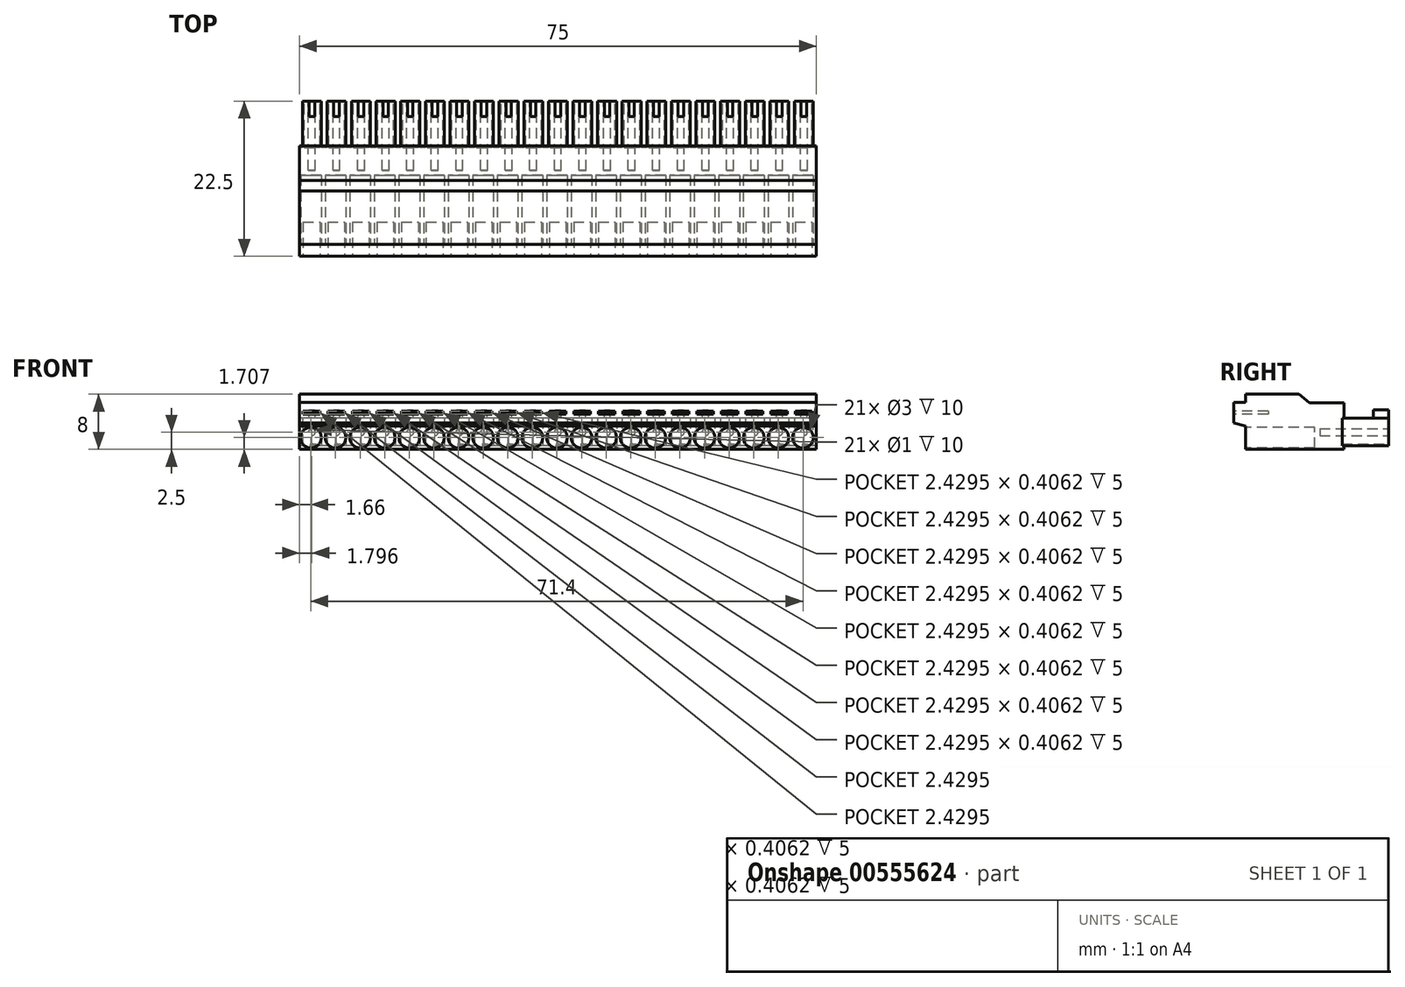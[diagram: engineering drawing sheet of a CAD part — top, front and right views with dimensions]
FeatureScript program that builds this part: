
annotation { "Feature Type Name" : "Feature", "Feature Type Description" : "" }
export const myFeature = defineFeature(function(context is Context, id is Id, definition is map)
    precondition{}
    {
        {
            var Q0;
            Q0=qCreatedBy(makeId("Right.planeOp"),FACE);
            var sketch = newSketch(context, id + "F0", { "sketchPlane" : qUnion([Q0])});
            skLineSegment(sketch, "E0", {"start": v(0, 0) * mm, "end": v(-14.25, 0) * mm});
            skLineSegment(sketch, "E1", {"start": v(-14.25, 0) * mm, "end": v(-14.25, 3.41) * mm});
            skLineSegment(sketch, "E2", {"start": v(-14.25, 8) * mm, "end": v(-6.5, 8) * mm});
            skLineSegment(sketch, "E3", {"start": v(0, 0) * mm, "end": v(0, 6.75) * mm});
            skLineSegment(sketch, "E4", {"start": v(0, 6.75) * mm, "end": v(-5, 6.75) * mm});
            skLineSegment(sketch, "E5", {"start": v(-5, 6.75) * mm, "end": v(-6.5, 8) * mm});
            skPoint(sketch, "E6.orphan", {"position": v(-5, 8) * mm});
            skLineSegment(sketch, "E7", {"start": v(-16, 3.83) * mm, "end": v(-16, 6.83) * mm});
            skLineSegment(sketch, "E8", {"start": v(-16, 6.83) * mm, "end": v(-14.25, 6.83) * mm});
            skLineSegment(sketch, "E9", {"start": v(-16, 3.83) * mm, "end": v(-14.25, 3.41) * mm});
            skLineSegment(sketch, "E10.trimOffspring", {"start": v(-14.25, 6.83) * mm, "end": v(-14.25, 8) * mm});
            skPoint(sketch, "E11.orphan", {"position": v(-14.25, 4) * mm});
            skLineSegment(sketch, "E12", {"start": v(0, 0) * mm, "end": v(0, 0.5) * mm});
            skLineSegment(sketch, "E13", {"start": v(0, 0.5) * mm, "end": v(6.5, 0.5) * mm});
            skLineSegment(sketch, "E14", {"start": v(6.5, 0.5) * mm, "end": v(6.5, 4.5) * mm});
            skLineSegment(sketch, "E15", {"start": v(6.5, 4.5) * mm, "end": v(0, 4.5) * mm});
            skSolve(sketch);
        }
        {
            var Q0;
            Q0 = qSketchRegion(id + "F0", true);
            extrude(context, id + "F1", {"entities" : qUnion([Q0]), "depth" : 75 * mm, "offsetDistance" : 25 * mm});
        }
        {
            var Q0;
            Q0=makeQuery(id+"F1.opExtrude","SWEPT_FACE",FACE,{"disambiguationData":[OSD([sQuery(id+"F0.wireOp",EDGE,"E1")])]});
            var sketch = newSketch(context, id + "F2", { "sketchPlane" : qUnion([Q0])});
            skLineSegment(sketch, "E16", {"start": v(0, 1.7) * mm, "end": v(75, 1.7) * mm, "construction": true});
            skCircle(sketch, "E17", {"center": v(1.66, 1.7) * mm, "radius": 1.5 * mm});
            skCircle(sketch, "E18.1.0.0", {"center": v(5.23, 1.7) * mm, "radius": 1.5 * mm});
            skCircle(sketch, "E18.2.0.0", {"center": v(8.8, 1.7) * mm, "radius": 1.5 * mm});
            skCircle(sketch, "E18.3.0.0", {"center": v(12.37, 1.7) * mm, "radius": 1.5 * mm});
            skCircle(sketch, "E18.4.0.0", {"center": v(15.94, 1.7) * mm, "radius": 1.5 * mm});
            skCircle(sketch, "E18.5.0.0", {"center": v(19.51, 1.7) * mm, "radius": 1.5 * mm});
            skCircle(sketch, "E18.6.0.0", {"center": v(23.08, 1.7) * mm, "radius": 1.5 * mm});
            skCircle(sketch, "E18.7.0.0", {"center": v(26.65, 1.7) * mm, "radius": 1.5 * mm});
            skCircle(sketch, "E18.8.0.0", {"center": v(30.22, 1.7) * mm, "radius": 1.5 * mm});
            skCircle(sketch, "E18.9.0.0", {"center": v(33.8, 1.7) * mm, "radius": 1.5 * mm});
            skCircle(sketch, "E18.10.0.0", {"center": v(37.36, 1.7) * mm, "radius": 1.5 * mm});
            skCircle(sketch, "E18.11.0.0", {"center": v(40.93, 1.7) * mm, "radius": 1.5 * mm});
            skCircle(sketch, "E18.12.0.0", {"center": v(44.5, 1.7) * mm, "radius": 1.5 * mm});
            skCircle(sketch, "E18.13.0.0", {"center": v(48.07, 1.7) * mm, "radius": 1.5 * mm});
            skCircle(sketch, "E18.14.0.0", {"center": v(51.64, 1.7) * mm, "radius": 1.5 * mm});
            skCircle(sketch, "E18.15.0.0", {"center": v(55.21, 1.7) * mm, "radius": 1.5 * mm});
            skCircle(sketch, "E18.16.0.0", {"center": v(58.78, 1.7) * mm, "radius": 1.5 * mm});
            skCircle(sketch, "E18.17.0.0", {"center": v(62.35, 1.7) * mm, "radius": 1.5 * mm});
            skCircle(sketch, "E18.18.0.0", {"center": v(65.92, 1.7) * mm, "radius": 1.5 * mm});
            skCircle(sketch, "E18.19.0.0", {"center": v(69.5, 1.7) * mm, "radius": 1.5 * mm});
            skCircle(sketch, "E18.20.0.0", {"center": v(73.06, 1.7) * mm, "radius": 1.5 * mm});
            skLineSegment(sketch, "E18.direction1", {"start": v(1.66, 1.7) * mm, "end": v(5.23, 1.7) * mm, "construction": true});
            skSolve(sketch);
        }
        {
            var Q0;
            Q0 = qSketchRegion(id + "F2", true);
            extrude(context, id + "F3", {"entities" : qUnion([Q0]), "operationType" : NewBodyOperationType.REMOVE, "oppositeDirection" : true, "depth" : 10 * mm, "offsetDistance" : 25 * mm});
        }
        {
            var Q0;
            Q0=makeQuery(id+"F1.opExtrude","SWEPT_FACE",FACE,{"disambiguationData":[OSD([sQuery(id+"F0.wireOp",EDGE,"E14")])]});
            var sketch = newSketch(context, id + "F4", { "sketchPlane" : qUnion([Q0])});
            skLineSegment(sketch, "E19", {"start": v(-75, 2.5) * mm, "end": v(0, 2.5) * mm, "construction": true});
            skCircle(sketch, "E20", {"center": v(-73.2, 2.5) * mm, "radius": 0.5 * mm});
            skCircle(sketch, "E21.1.0.0", {"center": v(-69.63, 2.5) * mm, "radius": 0.5 * mm});
            skCircle(sketch, "E21.2.0.0", {"center": v(-66.06, 2.5) * mm, "radius": 0.5 * mm});
            skCircle(sketch, "E21.3.0.0", {"center": v(-62.49, 2.5) * mm, "radius": 0.5 * mm});
            skCircle(sketch, "E21.4.0.0", {"center": v(-58.92, 2.5) * mm, "radius": 0.5 * mm});
            skCircle(sketch, "E21.5.0.0", {"center": v(-55.35, 2.5) * mm, "radius": 0.5 * mm});
            skCircle(sketch, "E21.6.0.0", {"center": v(-51.78, 2.5) * mm, "radius": 0.5 * mm});
            skCircle(sketch, "E21.7.0.0", {"center": v(-48.2, 2.5) * mm, "radius": 0.5 * mm});
            skCircle(sketch, "E21.8.0.0", {"center": v(-44.64, 2.5) * mm, "radius": 0.5 * mm});
            skCircle(sketch, "E21.9.0.0", {"center": v(-41.07, 2.5) * mm, "radius": 0.5 * mm});
            skCircle(sketch, "E21.10.0.0", {"center": v(-37.5, 2.5) * mm, "radius": 0.5 * mm});
            skCircle(sketch, "E21.11.0.0", {"center": v(-33.93, 2.5) * mm, "radius": 0.5 * mm});
            skCircle(sketch, "E21.12.0.0", {"center": v(-30.36, 2.5) * mm, "radius": 0.5 * mm});
            skCircle(sketch, "E21.13.0.0", {"center": v(-26.79, 2.5) * mm, "radius": 0.5 * mm});
            skCircle(sketch, "E21.14.0.0", {"center": v(-23.22, 2.5) * mm, "radius": 0.5 * mm});
            skCircle(sketch, "E21.15.0.0", {"center": v(-19.65, 2.5) * mm, "radius": 0.5 * mm});
            skCircle(sketch, "E21.16.0.0", {"center": v(-16.08, 2.5) * mm, "radius": 0.5 * mm});
            skCircle(sketch, "E21.17.0.0", {"center": v(-12.5, 2.5) * mm, "radius": 0.5 * mm});
            skCircle(sketch, "E21.18.0.0", {"center": v(-8.94, 2.5) * mm, "radius": 0.5 * mm});
            skCircle(sketch, "E21.19.0.0", {"center": v(-5.37, 2.5) * mm, "radius": 0.5 * mm});
            skCircle(sketch, "E21.20.0.0", {"center": v(-1.8, 2.5) * mm, "radius": 0.5 * mm});
            skLineSegment(sketch, "E21.direction1", {"start": v(-73.2, 2.5) * mm, "end": v(-69.63, 2.5) * mm, "construction": true});
            skSolve(sketch);
        }
        {
            var Q0;
            Q0 = qSketchRegion(id + "F4", true);
            extrude(context, id + "F5", {"entities" : qUnion([Q0]), "operationType" : NewBodyOperationType.REMOVE, "oppositeDirection" : true, "depth" : 10 * mm, "offsetDistance" : 25 * mm});
        }
        {
            var Q0;
            Q0=makeQuery(id+"F1.opExtrude","SWEPT_FACE",FACE,{"disambiguationData":[OSD([sQuery(id+"F0.wireOp",EDGE,"E14")])]});
            var sketch = newSketch(context, id + "F6", { "sketchPlane" : qUnion([Q0])});
            skLineSegment(sketch, "E22", {"start": v(-73.2, 2.5) * mm, "end": v(-73.2, 5.96) * mm, "construction": true});
            skLineSegment(sketch, "E23", {"start": v(-73.2, 5.96) * mm, "end": v(-73.2, 0.5) * mm, "construction": true});
            skLineSegment(sketch, "E24.left", {"start": v(-71.82, 4.5) * mm, "end": v(-71.82, 0.5) * mm});
            skPoint(sketch, "E24.middle", {"position": v(-73.2, 2.5) * mm});
            skArc(sketch, "E25", {"start": v(-72.09, 0.5) * mm, "mid": v(-73.23, 0.75) * mm, "end": v(-74.37, 0.5) * mm});
            skLineSegment(sketch, "E26.right", {"start": v(-71, 4.5) * mm, "end": v(-71, 0.5) * mm});
            skPoint(sketch, "E26.middle", {"position": v(-69.63, 2.5) * mm});
            skLineSegment(sketch, "E27.bottom", {"start": v(-71.82, 4.5) * mm, "end": v(-71, 4.5) * mm});
            skLineSegment(sketch, "E27.top", {"start": v(-71.82, 0.5) * mm, "end": v(-71, 0.5) * mm});
            skLineSegment(sketch, "E28", {"start": v(-74.37, 0.5) * mm, "end": v(-72.09, 0.5) * mm});
            skPoint(sketch, "E24.right.end.orphan", {"position": v(-74.57, 0.5) * mm});
            skPoint(sketch, "E24.bottom.end.orphan", {"position": v(-74.57, 4.5) * mm});
            skPoint(sketch, "E26.left.start.orphan", {"position": v(-68.25, 4.5) * mm});
            skPoint(sketch, "E26.top.start.orphan", {"position": v(-68.25, 0.5) * mm});
            skLineSegment(sketch, "E29.1.0.0", {"start": v(-67.43, 4.5) * mm, "end": v(-67.43, 0.5) * mm});
            skLineSegment(sketch, "E29.1.0.1", {"start": v(-68.25, 4.5) * mm, "end": v(-67.43, 4.5) * mm});
            skLineSegment(sketch, "E29.1.0.2", {"start": v(-68.25, 4.5) * mm, "end": v(-68.25, 0.5) * mm});
            skLineSegment(sketch, "E29.1.0.3", {"start": v(-68.25, 0.5) * mm, "end": v(-67.43, 0.5) * mm});
            skLineSegment(sketch, "E29.1.0.4", {"start": v(-67.43, 4.5) * mm, "end": v(-67.43, 0.5) * mm});
            skLineSegment(sketch, "E29.1.0.5", {"start": v(-68.25, 4.5) * mm, "end": v(-68.25, 0.5) * mm});
            skArc(sketch, "E29.1.0.6", {"start": v(-68.52, 0.5) * mm, "mid": v(-69.66, 0.75) * mm, "end": v(-70.8, 0.5) * mm});
            skLineSegment(sketch, "E29.1.0.7", {"start": v(-70.8, 0.5) * mm, "end": v(-68.52, 0.5) * mm});
            skLineSegment(sketch, "E29.2.0.0", {"start": v(-63.86, 4.5) * mm, "end": v(-63.86, 0.5) * mm});
            skLineSegment(sketch, "E29.2.0.1", {"start": v(-64.68, 4.5) * mm, "end": v(-63.86, 4.5) * mm});
            skLineSegment(sketch, "E29.2.0.2", {"start": v(-64.68, 4.5) * mm, "end": v(-64.68, 0.5) * mm});
            skLineSegment(sketch, "E29.2.0.3", {"start": v(-64.68, 0.5) * mm, "end": v(-63.86, 0.5) * mm});
            skLineSegment(sketch, "E29.2.0.4", {"start": v(-63.86, 4.5) * mm, "end": v(-63.86, 0.5) * mm});
            skLineSegment(sketch, "E29.2.0.5", {"start": v(-64.68, 4.5) * mm, "end": v(-64.68, 0.5) * mm});
            skArc(sketch, "E29.2.0.6", {"start": v(-64.95, 0.5) * mm, "mid": v(-66.09, 0.75) * mm, "end": v(-67.23, 0.5) * mm});
            skLineSegment(sketch, "E29.2.0.7", {"start": v(-67.23, 0.5) * mm, "end": v(-64.95, 0.5) * mm});
            skLineSegment(sketch, "E29.3.0.0", {"start": v(-60.3, 4.5) * mm, "end": v(-60.3, 0.5) * mm});
            skLineSegment(sketch, "E29.3.0.1", {"start": v(-61.11, 4.5) * mm, "end": v(-60.3, 4.5) * mm});
            skLineSegment(sketch, "E29.3.0.2", {"start": v(-61.11, 4.5) * mm, "end": v(-61.11, 0.5) * mm});
            skLineSegment(sketch, "E29.3.0.3", {"start": v(-61.11, 0.5) * mm, "end": v(-60.3, 0.5) * mm});
            skLineSegment(sketch, "E29.3.0.4", {"start": v(-60.3, 4.5) * mm, "end": v(-60.3, 0.5) * mm});
            skLineSegment(sketch, "E29.3.0.5", {"start": v(-61.11, 4.5) * mm, "end": v(-61.11, 0.5) * mm});
            skArc(sketch, "E29.3.0.6", {"start": v(-61.38, 0.5) * mm, "mid": v(-62.52, 0.75) * mm, "end": v(-63.66, 0.5) * mm});
            skLineSegment(sketch, "E29.3.0.7", {"start": v(-63.66, 0.5) * mm, "end": v(-61.38, 0.5) * mm});
            skLineSegment(sketch, "E29.4.0.0", {"start": v(-56.72, 4.5) * mm, "end": v(-56.72, 0.5) * mm});
            skLineSegment(sketch, "E29.4.0.1", {"start": v(-57.54, 4.5) * mm, "end": v(-56.72, 4.5) * mm});
            skLineSegment(sketch, "E29.4.0.2", {"start": v(-57.54, 4.5) * mm, "end": v(-57.54, 0.5) * mm});
            skLineSegment(sketch, "E29.4.0.3", {"start": v(-57.54, 0.5) * mm, "end": v(-56.72, 0.5) * mm});
            skLineSegment(sketch, "E29.4.0.4", {"start": v(-56.72, 4.5) * mm, "end": v(-56.72, 0.5) * mm});
            skLineSegment(sketch, "E29.4.0.5", {"start": v(-57.54, 4.5) * mm, "end": v(-57.54, 0.5) * mm});
            skArc(sketch, "E29.4.0.6", {"start": v(-57.8, 0.5) * mm, "mid": v(-58.95, 0.75) * mm, "end": v(-60.1, 0.5) * mm});
            skLineSegment(sketch, "E29.4.0.7", {"start": v(-60.1, 0.5) * mm, "end": v(-57.8, 0.5) * mm});
            skLineSegment(sketch, "E29.5.0.0", {"start": v(-53.15, 4.5) * mm, "end": v(-53.15, 0.5) * mm});
            skLineSegment(sketch, "E29.5.0.1", {"start": v(-53.97, 4.5) * mm, "end": v(-53.15, 4.5) * mm});
            skLineSegment(sketch, "E29.5.0.2", {"start": v(-53.97, 4.5) * mm, "end": v(-53.97, 0.5) * mm});
            skLineSegment(sketch, "E29.5.0.3", {"start": v(-53.97, 0.5) * mm, "end": v(-53.15, 0.5) * mm});
            skLineSegment(sketch, "E29.5.0.4", {"start": v(-53.15, 4.5) * mm, "end": v(-53.15, 0.5) * mm});
            skLineSegment(sketch, "E29.5.0.5", {"start": v(-53.97, 4.5) * mm, "end": v(-53.97, 0.5) * mm});
            skArc(sketch, "E29.5.0.6", {"start": v(-54.24, 0.5) * mm, "mid": v(-55.38, 0.75) * mm, "end": v(-56.52, 0.5) * mm});
            skLineSegment(sketch, "E29.5.0.7", {"start": v(-56.52, 0.5) * mm, "end": v(-54.24, 0.5) * mm});
            skLineSegment(sketch, "E29.6.0.0", {"start": v(-49.58, 4.5) * mm, "end": v(-49.58, 0.5) * mm});
            skLineSegment(sketch, "E29.6.0.1", {"start": v(-50.4, 4.5) * mm, "end": v(-49.58, 4.5) * mm});
            skLineSegment(sketch, "E29.6.0.2", {"start": v(-50.4, 4.5) * mm, "end": v(-50.4, 0.5) * mm});
            skLineSegment(sketch, "E29.6.0.3", {"start": v(-50.4, 0.5) * mm, "end": v(-49.58, 0.5) * mm});
            skLineSegment(sketch, "E29.6.0.4", {"start": v(-49.58, 4.5) * mm, "end": v(-49.58, 0.5) * mm});
            skLineSegment(sketch, "E29.6.0.5", {"start": v(-50.4, 4.5) * mm, "end": v(-50.4, 0.5) * mm});
            skArc(sketch, "E29.6.0.6", {"start": v(-50.67, 0.5) * mm, "mid": v(-51.8, 0.75) * mm, "end": v(-52.95, 0.5) * mm});
            skLineSegment(sketch, "E29.6.0.7", {"start": v(-52.95, 0.5) * mm, "end": v(-50.67, 0.5) * mm});
            skLineSegment(sketch, "E29.7.0.0", {"start": v(-46.01, 4.5) * mm, "end": v(-46.01, 0.5) * mm});
            skLineSegment(sketch, "E29.7.0.1", {"start": v(-46.83, 4.5) * mm, "end": v(-46.01, 4.5) * mm});
            skLineSegment(sketch, "E29.7.0.2", {"start": v(-46.83, 4.5) * mm, "end": v(-46.83, 0.5) * mm});
            skLineSegment(sketch, "E29.7.0.3", {"start": v(-46.83, 0.5) * mm, "end": v(-46.01, 0.5) * mm});
            skLineSegment(sketch, "E29.7.0.4", {"start": v(-46.01, 4.5) * mm, "end": v(-46.01, 0.5) * mm});
            skLineSegment(sketch, "E29.7.0.5", {"start": v(-46.83, 4.5) * mm, "end": v(-46.83, 0.5) * mm});
            skArc(sketch, "E29.7.0.6", {"start": v(-47.1, 0.5) * mm, "mid": v(-48.24, 0.75) * mm, "end": v(-49.38, 0.5) * mm});
            skLineSegment(sketch, "E29.7.0.7", {"start": v(-49.38, 0.5) * mm, "end": v(-47.1, 0.5) * mm});
            skLineSegment(sketch, "E29.8.0.0", {"start": v(-42.44, 4.5) * mm, "end": v(-42.44, 0.5) * mm});
            skLineSegment(sketch, "E29.8.0.1", {"start": v(-43.26, 4.5) * mm, "end": v(-42.44, 4.5) * mm});
            skLineSegment(sketch, "E29.8.0.2", {"start": v(-43.26, 4.5) * mm, "end": v(-43.26, 0.5) * mm});
            skLineSegment(sketch, "E29.8.0.3", {"start": v(-43.26, 0.5) * mm, "end": v(-42.44, 0.5) * mm});
            skLineSegment(sketch, "E29.8.0.4", {"start": v(-42.44, 4.5) * mm, "end": v(-42.44, 0.5) * mm});
            skLineSegment(sketch, "E29.8.0.5", {"start": v(-43.26, 4.5) * mm, "end": v(-43.26, 0.5) * mm});
            skArc(sketch, "E29.8.0.6", {"start": v(-43.53, 0.5) * mm, "mid": v(-44.67, 0.75) * mm, "end": v(-45.81, 0.5) * mm});
            skLineSegment(sketch, "E29.8.0.7", {"start": v(-45.81, 0.5) * mm, "end": v(-43.53, 0.5) * mm});
            skLineSegment(sketch, "E29.9.0.0", {"start": v(-38.87, 4.5) * mm, "end": v(-38.87, 0.5) * mm});
            skLineSegment(sketch, "E29.9.0.1", {"start": v(-39.7, 4.5) * mm, "end": v(-38.87, 4.5) * mm});
            skLineSegment(sketch, "E29.9.0.2", {"start": v(-39.7, 4.5) * mm, "end": v(-39.7, 0.5) * mm});
            skLineSegment(sketch, "E29.9.0.3", {"start": v(-39.7, 0.5) * mm, "end": v(-38.87, 0.5) * mm});
            skLineSegment(sketch, "E29.9.0.4", {"start": v(-38.87, 4.5) * mm, "end": v(-38.87, 0.5) * mm});
            skLineSegment(sketch, "E29.9.0.5", {"start": v(-39.7, 4.5) * mm, "end": v(-39.7, 0.5) * mm});
            skArc(sketch, "E29.9.0.6", {"start": v(-39.96, 0.5) * mm, "mid": v(-41.1, 0.75) * mm, "end": v(-42.24, 0.5) * mm});
            skLineSegment(sketch, "E29.9.0.7", {"start": v(-42.24, 0.5) * mm, "end": v(-39.96, 0.5) * mm});
            skLineSegment(sketch, "E29.10.0.0", {"start": v(-35.3, 4.5) * mm, "end": v(-35.3, 0.5) * mm});
            skLineSegment(sketch, "E29.10.0.1", {"start": v(-36.12, 4.5) * mm, "end": v(-35.3, 4.5) * mm});
            skLineSegment(sketch, "E29.10.0.2", {"start": v(-36.12, 4.5) * mm, "end": v(-36.12, 0.5) * mm});
            skLineSegment(sketch, "E29.10.0.3", {"start": v(-36.12, 0.5) * mm, "end": v(-35.3, 0.5) * mm});
            skLineSegment(sketch, "E29.10.0.4", {"start": v(-35.3, 4.5) * mm, "end": v(-35.3, 0.5) * mm});
            skLineSegment(sketch, "E29.10.0.5", {"start": v(-36.12, 4.5) * mm, "end": v(-36.12, 0.5) * mm});
            skArc(sketch, "E29.10.0.6", {"start": v(-36.39, 0.5) * mm, "mid": v(-37.53, 0.75) * mm, "end": v(-38.67, 0.5) * mm});
            skLineSegment(sketch, "E29.10.0.7", {"start": v(-38.67, 0.5) * mm, "end": v(-36.39, 0.5) * mm});
            skLineSegment(sketch, "E29.11.0.0", {"start": v(-31.73, 4.5) * mm, "end": v(-31.73, 0.5) * mm});
            skLineSegment(sketch, "E29.11.0.1", {"start": v(-32.55, 4.5) * mm, "end": v(-31.73, 4.5) * mm});
            skLineSegment(sketch, "E29.11.0.2", {"start": v(-32.55, 4.5) * mm, "end": v(-32.55, 0.5) * mm});
            skLineSegment(sketch, "E29.11.0.3", {"start": v(-32.55, 0.5) * mm, "end": v(-31.73, 0.5) * mm});
            skLineSegment(sketch, "E29.11.0.4", {"start": v(-31.73, 4.5) * mm, "end": v(-31.73, 0.5) * mm});
            skLineSegment(sketch, "E29.11.0.5", {"start": v(-32.55, 4.5) * mm, "end": v(-32.55, 0.5) * mm});
            skArc(sketch, "E29.11.0.6", {"start": v(-32.82, 0.5) * mm, "mid": v(-33.96, 0.75) * mm, "end": v(-35.1, 0.5) * mm});
            skLineSegment(sketch, "E29.11.0.7", {"start": v(-35.1, 0.5) * mm, "end": v(-32.82, 0.5) * mm});
            skLineSegment(sketch, "E29.12.0.0", {"start": v(-28.16, 4.5) * mm, "end": v(-28.16, 0.5) * mm});
            skLineSegment(sketch, "E29.12.0.1", {"start": v(-28.98, 4.5) * mm, "end": v(-28.16, 4.5) * mm});
            skLineSegment(sketch, "E29.12.0.2", {"start": v(-28.98, 4.5) * mm, "end": v(-28.98, 0.5) * mm});
            skLineSegment(sketch, "E29.12.0.3", {"start": v(-28.98, 0.5) * mm, "end": v(-28.16, 0.5) * mm});
            skLineSegment(sketch, "E29.12.0.4", {"start": v(-28.16, 4.5) * mm, "end": v(-28.16, 0.5) * mm});
            skLineSegment(sketch, "E29.12.0.5", {"start": v(-28.98, 4.5) * mm, "end": v(-28.98, 0.5) * mm});
            skArc(sketch, "E29.12.0.6", {"start": v(-29.25, 0.5) * mm, "mid": v(-30.39, 0.75) * mm, "end": v(-31.53, 0.5) * mm});
            skLineSegment(sketch, "E29.12.0.7", {"start": v(-31.53, 0.5) * mm, "end": v(-29.25, 0.5) * mm});
            skLineSegment(sketch, "E29.13.0.0", {"start": v(-24.6, 4.5) * mm, "end": v(-24.6, 0.5) * mm});
            skLineSegment(sketch, "E29.13.0.1", {"start": v(-25.41, 4.5) * mm, "end": v(-24.6, 4.5) * mm});
            skLineSegment(sketch, "E29.13.0.2", {"start": v(-25.41, 4.5) * mm, "end": v(-25.41, 0.5) * mm});
            skLineSegment(sketch, "E29.13.0.3", {"start": v(-25.41, 0.5) * mm, "end": v(-24.6, 0.5) * mm});
            skLineSegment(sketch, "E29.13.0.4", {"start": v(-24.6, 4.5) * mm, "end": v(-24.6, 0.5) * mm});
            skLineSegment(sketch, "E29.13.0.5", {"start": v(-25.41, 4.5) * mm, "end": v(-25.41, 0.5) * mm});
            skArc(sketch, "E29.13.0.6", {"start": v(-25.68, 0.5) * mm, "mid": v(-26.82, 0.75) * mm, "end": v(-27.96, 0.5) * mm});
            skLineSegment(sketch, "E29.13.0.7", {"start": v(-27.96, 0.5) * mm, "end": v(-25.68, 0.5) * mm});
            skLineSegment(sketch, "E29.14.0.0", {"start": v(-21.02, 4.5) * mm, "end": v(-21.02, 0.5) * mm});
            skLineSegment(sketch, "E29.14.0.1", {"start": v(-21.84, 4.5) * mm, "end": v(-21.02, 4.5) * mm});
            skLineSegment(sketch, "E29.14.0.2", {"start": v(-21.84, 4.5) * mm, "end": v(-21.84, 0.5) * mm});
            skLineSegment(sketch, "E29.14.0.3", {"start": v(-21.84, 0.5) * mm, "end": v(-21.02, 0.5) * mm});
            skLineSegment(sketch, "E29.14.0.4", {"start": v(-21.02, 4.5) * mm, "end": v(-21.02, 0.5) * mm});
            skLineSegment(sketch, "E29.14.0.5", {"start": v(-21.84, 4.5) * mm, "end": v(-21.84, 0.5) * mm});
            skArc(sketch, "E29.14.0.6", {"start": v(-22.1, 0.5) * mm, "mid": v(-23.25, 0.75) * mm, "end": v(-24.4, 0.5) * mm});
            skLineSegment(sketch, "E29.14.0.7", {"start": v(-24.4, 0.5) * mm, "end": v(-22.1, 0.5) * mm});
            skLineSegment(sketch, "E29.15.0.0", {"start": v(-17.45, 4.5) * mm, "end": v(-17.45, 0.5) * mm});
            skLineSegment(sketch, "E29.15.0.1", {"start": v(-18.27, 4.5) * mm, "end": v(-17.45, 4.5) * mm});
            skLineSegment(sketch, "E29.15.0.2", {"start": v(-18.27, 4.5) * mm, "end": v(-18.27, 0.5) * mm});
            skLineSegment(sketch, "E29.15.0.3", {"start": v(-18.27, 0.5) * mm, "end": v(-17.45, 0.5) * mm});
            skLineSegment(sketch, "E29.15.0.4", {"start": v(-17.45, 4.5) * mm, "end": v(-17.45, 0.5) * mm});
            skLineSegment(sketch, "E29.15.0.5", {"start": v(-18.27, 4.5) * mm, "end": v(-18.27, 0.5) * mm});
            skArc(sketch, "E29.15.0.6", {"start": v(-18.54, 0.5) * mm, "mid": v(-19.68, 0.75) * mm, "end": v(-20.82, 0.5) * mm});
            skLineSegment(sketch, "E29.15.0.7", {"start": v(-20.82, 0.5) * mm, "end": v(-18.54, 0.5) * mm});
            skLineSegment(sketch, "E29.16.0.0", {"start": v(-13.88, 4.5) * mm, "end": v(-13.88, 0.5) * mm});
            skLineSegment(sketch, "E29.16.0.1", {"start": v(-14.7, 4.5) * mm, "end": v(-13.88, 4.5) * mm});
            skLineSegment(sketch, "E29.16.0.2", {"start": v(-14.7, 4.5) * mm, "end": v(-14.7, 0.5) * mm});
            skLineSegment(sketch, "E29.16.0.3", {"start": v(-14.7, 0.5) * mm, "end": v(-13.88, 0.5) * mm});
            skLineSegment(sketch, "E29.16.0.4", {"start": v(-13.88, 4.5) * mm, "end": v(-13.88, 0.5) * mm});
            skLineSegment(sketch, "E29.16.0.5", {"start": v(-14.7, 4.5) * mm, "end": v(-14.7, 0.5) * mm});
            skArc(sketch, "E29.16.0.6", {"start": v(-14.97, 0.5) * mm, "mid": v(-16.1, 0.75) * mm, "end": v(-17.25, 0.5) * mm});
            skLineSegment(sketch, "E29.16.0.7", {"start": v(-17.25, 0.5) * mm, "end": v(-14.97, 0.5) * mm});
            skLineSegment(sketch, "E29.17.0.0", {"start": v(-10.31, 4.5) * mm, "end": v(-10.31, 0.5) * mm});
            skLineSegment(sketch, "E29.17.0.1", {"start": v(-11.13, 4.5) * mm, "end": v(-10.31, 4.5) * mm});
            skLineSegment(sketch, "E29.17.0.2", {"start": v(-11.13, 4.5) * mm, "end": v(-11.13, 0.5) * mm});
            skLineSegment(sketch, "E29.17.0.3", {"start": v(-11.13, 0.5) * mm, "end": v(-10.31, 0.5) * mm});
            skLineSegment(sketch, "E29.17.0.4", {"start": v(-10.31, 4.5) * mm, "end": v(-10.31, 0.5) * mm});
            skLineSegment(sketch, "E29.17.0.5", {"start": v(-11.13, 4.5) * mm, "end": v(-11.13, 0.5) * mm});
            skArc(sketch, "E29.17.0.6", {"start": v(-11.4, 0.5) * mm, "mid": v(-12.54, 0.75) * mm, "end": v(-13.68, 0.5) * mm});
            skLineSegment(sketch, "E29.17.0.7", {"start": v(-13.68, 0.5) * mm, "end": v(-11.4, 0.5) * mm});
            skLineSegment(sketch, "E29.18.0.0", {"start": v(-6.74, 4.5) * mm, "end": v(-6.74, 0.5) * mm});
            skLineSegment(sketch, "E29.18.0.1", {"start": v(-7.56, 4.5) * mm, "end": v(-6.74, 4.5) * mm});
            skLineSegment(sketch, "E29.18.0.2", {"start": v(-7.56, 4.5) * mm, "end": v(-7.56, 0.5) * mm});
            skLineSegment(sketch, "E29.18.0.3", {"start": v(-7.56, 0.5) * mm, "end": v(-6.74, 0.5) * mm});
            skLineSegment(sketch, "E29.18.0.4", {"start": v(-6.74, 4.5) * mm, "end": v(-6.74, 0.5) * mm});
            skLineSegment(sketch, "E29.18.0.5", {"start": v(-7.56, 4.5) * mm, "end": v(-7.56, 0.5) * mm});
            skArc(sketch, "E29.18.0.6", {"start": v(-7.83, 0.5) * mm, "mid": v(-8.97, 0.75) * mm, "end": v(-10.11, 0.5) * mm});
            skLineSegment(sketch, "E29.18.0.7", {"start": v(-10.11, 0.5) * mm, "end": v(-7.83, 0.5) * mm});
            skLineSegment(sketch, "E29.19.0.0", {"start": v(-3.17, 4.5) * mm, "end": v(-3.17, 0.5) * mm});
            skLineSegment(sketch, "E29.19.0.1", {"start": v(-4, 4.5) * mm, "end": v(-3.17, 4.5) * mm});
            skLineSegment(sketch, "E29.19.0.2", {"start": v(-4, 4.5) * mm, "end": v(-4, 0.5) * mm});
            skLineSegment(sketch, "E29.19.0.3", {"start": v(-4, 0.5) * mm, "end": v(-3.17, 0.5) * mm});
            skLineSegment(sketch, "E29.19.0.4", {"start": v(-3.17, 4.5) * mm, "end": v(-3.17, 0.5) * mm});
            skLineSegment(sketch, "E29.19.0.5", {"start": v(-4, 4.5) * mm, "end": v(-4, 0.5) * mm});
            skArc(sketch, "E29.19.0.6", {"start": v(-4.26, 0.5) * mm, "mid": v(-5.4, 0.75) * mm, "end": v(-6.54, 0.5) * mm});
            skLineSegment(sketch, "E29.19.0.7", {"start": v(-6.54, 0.5) * mm, "end": v(-4.26, 0.5) * mm});
            skLineSegment(sketch, "E29.20.0.0", {"start": v(0.4, 4.5) * mm, "end": v(0.4, 0.5) * mm});
            skLineSegment(sketch, "E29.20.0.1", {"start": v(-0.42, 4.5) * mm, "end": v(0.4, 4.5) * mm});
            skLineSegment(sketch, "E29.20.0.2", {"start": v(-0.42, 4.5) * mm, "end": v(-0.42, 0.5) * mm});
            skLineSegment(sketch, "E29.20.0.3", {"start": v(-0.42, 0.5) * mm, "end": v(0.4, 0.5) * mm});
            skLineSegment(sketch, "E29.20.0.4", {"start": v(0.4, 4.5) * mm, "end": v(0.4, 0.5) * mm});
            skLineSegment(sketch, "E29.20.0.5", {"start": v(-0.42, 4.5) * mm, "end": v(-0.42, 0.5) * mm});
            skArc(sketch, "E29.20.0.6", {"start": v(-0.69, 0.5) * mm, "mid": v(-1.83, 0.75) * mm, "end": v(-2.97, 0.5) * mm});
            skLineSegment(sketch, "E29.20.0.7", {"start": v(-2.97, 0.5) * mm, "end": v(-0.69, 0.5) * mm});
            skLineSegment(sketch, "E29.direction1", {"start": v(-71.82, 0.5) * mm, "end": v(-68.25, 0.5) * mm, "construction": true});
            skLineSegment(sketch, "E30.bottom", {"start": v(-74.57, 0.5) * mm, "end": v(-75, 0.5) * mm});
            skLineSegment(sketch, "E30.top", {"start": v(-74.57, 4.5) * mm, "end": v(-75, 4.5) * mm});
            skLineSegment(sketch, "E30.left", {"start": v(-74.57, 0.5) * mm, "end": v(-74.57, 4.5) * mm});
            skLineSegment(sketch, "E30.right", {"start": v(-75, 0.5) * mm, "end": v(-75, 4.5) * mm});
            skSolve(sketch);
        }
        {
            var Q0;
            Q0 = qSketchRegion(id + "F6", true);
            extrude(context, id + "F7", {"entities" : qUnion([Q0]), "operationType" : NewBodyOperationType.REMOVE, "oppositeDirection" : true, "depth" : 6.75 * mm, "offsetDistance" : 25 * mm});
        }
        {
            var Q0;
            Q0=makeQuery(id+"F7.boolean.opBoolean","SPLIT",FACE,{"disambiguationData":[TD([makeQuery(id+"F5.boolean.opBoolean","COPY",FACE,{"derivedFrom":makeQuery(id+"F5.opExtrude","SWEPT_FACE",FACE,{"disambiguationData":[OSD([sQuery(id+"F4.wireOp",EDGE,"E20")])]})})])],"derivedFrom":makeQuery(id+"F1.opExtrude","SWEPT_FACE",FACE,{"disambiguationData":[OSD([sQuery(id+"F0.wireOp",EDGE,"E14")])]})});
            var sketch = newSketch(context, id + "F8", { "sketchPlane" : qUnion([Q0])});
            skLineSegment(sketch, "E31", {"start": v(-73.2, 2.5) * mm, "end": v(-73.2, 4.5) * mm, "construction": true});
            skLineSegment(sketch, "E32", {"start": v(-73.2, 4.5) * mm, "end": v(-73.2, 5.75) * mm, "construction": true});
            skLineSegment(sketch, "E33", {"start": v(-73.2, 5.75) * mm, "end": v(-73.6, 5.75) * mm});
            skLineSegment(sketch, "E34", {"start": v(-73.6, 5.75) * mm, "end": v(-73.6, 4.5) * mm});
            skLineSegment(sketch, "E35", {"start": v(-73.6, 4.5) * mm, "end": v(-72.8, 4.5) * mm});
            skLineSegment(sketch, "E36", {"start": v(-72.8, 4.5) * mm, "end": v(-72.8, 5.75) * mm});
            skLineSegment(sketch, "E37", {"start": v(-72.8, 5.75) * mm, "end": v(-73.2, 5.75) * mm});
            skLineSegment(sketch, "E38.1.0.0", {"start": v(-69.23, 5.75) * mm, "end": v(-69.63, 5.75) * mm});
            skLineSegment(sketch, "E38.1.0.1", {"start": v(-69.63, 5.75) * mm, "end": v(-70.03, 5.75) * mm});
            skLineSegment(sketch, "E38.1.0.2", {"start": v(-70.03, 5.75) * mm, "end": v(-70.03, 4.5) * mm});
            skLineSegment(sketch, "E38.1.0.3", {"start": v(-69.23, 4.5) * mm, "end": v(-69.23, 5.75) * mm});
            skLineSegment(sketch, "E38.1.0.4", {"start": v(-70.03, 4.5) * mm, "end": v(-69.23, 4.5) * mm});
            skLineSegment(sketch, "E38.2.0.0", {"start": v(-65.66, 5.75) * mm, "end": v(-66.06, 5.75) * mm});
            skLineSegment(sketch, "E38.2.0.1", {"start": v(-66.06, 5.75) * mm, "end": v(-66.46, 5.75) * mm});
            skLineSegment(sketch, "E38.2.0.2", {"start": v(-66.46, 5.75) * mm, "end": v(-66.46, 4.5) * mm});
            skLineSegment(sketch, "E38.2.0.3", {"start": v(-65.66, 4.5) * mm, "end": v(-65.66, 5.75) * mm});
            skLineSegment(sketch, "E38.2.0.4", {"start": v(-66.46, 4.5) * mm, "end": v(-65.66, 4.5) * mm});
            skLineSegment(sketch, "E38.3.0.0", {"start": v(-62.09, 5.75) * mm, "end": v(-62.49, 5.75) * mm});
            skLineSegment(sketch, "E38.3.0.1", {"start": v(-62.49, 5.75) * mm, "end": v(-62.89, 5.75) * mm});
            skLineSegment(sketch, "E38.3.0.2", {"start": v(-62.89, 5.75) * mm, "end": v(-62.89, 4.5) * mm});
            skLineSegment(sketch, "E38.3.0.3", {"start": v(-62.09, 4.5) * mm, "end": v(-62.09, 5.75) * mm});
            skLineSegment(sketch, "E38.3.0.4", {"start": v(-62.89, 4.5) * mm, "end": v(-62.09, 4.5) * mm});
            skLineSegment(sketch, "E38.4.0.0", {"start": v(-58.52, 5.75) * mm, "end": v(-58.92, 5.75) * mm});
            skLineSegment(sketch, "E38.4.0.1", {"start": v(-58.92, 5.75) * mm, "end": v(-59.32, 5.75) * mm});
            skLineSegment(sketch, "E38.4.0.2", {"start": v(-59.32, 5.75) * mm, "end": v(-59.32, 4.5) * mm});
            skLineSegment(sketch, "E38.4.0.3", {"start": v(-58.52, 4.5) * mm, "end": v(-58.52, 5.75) * mm});
            skLineSegment(sketch, "E38.4.0.4", {"start": v(-59.32, 4.5) * mm, "end": v(-58.52, 4.5) * mm});
            skLineSegment(sketch, "E38.5.0.0", {"start": v(-54.95, 5.75) * mm, "end": v(-55.35, 5.75) * mm});
            skLineSegment(sketch, "E38.5.0.1", {"start": v(-55.35, 5.75) * mm, "end": v(-55.75, 5.75) * mm});
            skLineSegment(sketch, "E38.5.0.2", {"start": v(-55.75, 5.75) * mm, "end": v(-55.75, 4.5) * mm});
            skLineSegment(sketch, "E38.5.0.3", {"start": v(-54.95, 4.5) * mm, "end": v(-54.95, 5.75) * mm});
            skLineSegment(sketch, "E38.5.0.4", {"start": v(-55.75, 4.5) * mm, "end": v(-54.95, 4.5) * mm});
            skLineSegment(sketch, "E38.6.0.0", {"start": v(-51.38, 5.75) * mm, "end": v(-51.78, 5.75) * mm});
            skLineSegment(sketch, "E38.6.0.1", {"start": v(-51.78, 5.75) * mm, "end": v(-52.18, 5.75) * mm});
            skLineSegment(sketch, "E38.6.0.2", {"start": v(-52.18, 5.75) * mm, "end": v(-52.18, 4.5) * mm});
            skLineSegment(sketch, "E38.6.0.3", {"start": v(-51.38, 4.5) * mm, "end": v(-51.38, 5.75) * mm});
            skLineSegment(sketch, "E38.6.0.4", {"start": v(-52.18, 4.5) * mm, "end": v(-51.38, 4.5) * mm});
            skLineSegment(sketch, "E38.7.0.0", {"start": v(-47.8, 5.75) * mm, "end": v(-48.2, 5.75) * mm});
            skLineSegment(sketch, "E38.7.0.1", {"start": v(-48.2, 5.75) * mm, "end": v(-48.6, 5.75) * mm});
            skLineSegment(sketch, "E38.7.0.2", {"start": v(-48.6, 5.75) * mm, "end": v(-48.6, 4.5) * mm});
            skLineSegment(sketch, "E38.7.0.3", {"start": v(-47.8, 4.5) * mm, "end": v(-47.8, 5.75) * mm});
            skLineSegment(sketch, "E38.7.0.4", {"start": v(-48.6, 4.5) * mm, "end": v(-47.8, 4.5) * mm});
            skLineSegment(sketch, "E38.8.0.0", {"start": v(-44.24, 5.75) * mm, "end": v(-44.64, 5.75) * mm});
            skLineSegment(sketch, "E38.8.0.1", {"start": v(-44.64, 5.75) * mm, "end": v(-45.04, 5.75) * mm});
            skLineSegment(sketch, "E38.8.0.2", {"start": v(-45.04, 5.75) * mm, "end": v(-45.04, 4.5) * mm});
            skLineSegment(sketch, "E38.8.0.3", {"start": v(-44.24, 4.5) * mm, "end": v(-44.24, 5.75) * mm});
            skLineSegment(sketch, "E38.8.0.4", {"start": v(-45.04, 4.5) * mm, "end": v(-44.24, 4.5) * mm});
            skLineSegment(sketch, "E38.9.0.0", {"start": v(-40.67, 5.75) * mm, "end": v(-41.07, 5.75) * mm});
            skLineSegment(sketch, "E38.9.0.1", {"start": v(-41.07, 5.75) * mm, "end": v(-41.47, 5.75) * mm});
            skLineSegment(sketch, "E38.9.0.2", {"start": v(-41.47, 5.75) * mm, "end": v(-41.47, 4.5) * mm});
            skLineSegment(sketch, "E38.9.0.3", {"start": v(-40.67, 4.5) * mm, "end": v(-40.67, 5.75) * mm});
            skLineSegment(sketch, "E38.9.0.4", {"start": v(-41.47, 4.5) * mm, "end": v(-40.67, 4.5) * mm});
            skLineSegment(sketch, "E38.10.0.0", {"start": v(-37.1, 5.75) * mm, "end": v(-37.5, 5.75) * mm});
            skLineSegment(sketch, "E38.10.0.1", {"start": v(-37.5, 5.75) * mm, "end": v(-37.9, 5.75) * mm});
            skLineSegment(sketch, "E38.10.0.2", {"start": v(-37.9, 5.75) * mm, "end": v(-37.9, 4.5) * mm});
            skLineSegment(sketch, "E38.10.0.3", {"start": v(-37.1, 4.5) * mm, "end": v(-37.1, 5.75) * mm});
            skLineSegment(sketch, "E38.10.0.4", {"start": v(-37.9, 4.5) * mm, "end": v(-37.1, 4.5) * mm});
            skLineSegment(sketch, "E38.11.0.0", {"start": v(-33.53, 5.75) * mm, "end": v(-33.93, 5.75) * mm});
            skLineSegment(sketch, "E38.11.0.1", {"start": v(-33.93, 5.75) * mm, "end": v(-34.33, 5.75) * mm});
            skLineSegment(sketch, "E38.11.0.2", {"start": v(-34.33, 5.75) * mm, "end": v(-34.33, 4.5) * mm});
            skLineSegment(sketch, "E38.11.0.3", {"start": v(-33.53, 4.5) * mm, "end": v(-33.53, 5.75) * mm});
            skLineSegment(sketch, "E38.11.0.4", {"start": v(-34.33, 4.5) * mm, "end": v(-33.53, 4.5) * mm});
            skLineSegment(sketch, "E38.12.0.0", {"start": v(-29.96, 5.75) * mm, "end": v(-30.36, 5.75) * mm});
            skLineSegment(sketch, "E38.12.0.1", {"start": v(-30.36, 5.75) * mm, "end": v(-30.76, 5.75) * mm});
            skLineSegment(sketch, "E38.12.0.2", {"start": v(-30.76, 5.75) * mm, "end": v(-30.76, 4.5) * mm});
            skLineSegment(sketch, "E38.12.0.3", {"start": v(-29.96, 4.5) * mm, "end": v(-29.96, 5.75) * mm});
            skLineSegment(sketch, "E38.12.0.4", {"start": v(-30.76, 4.5) * mm, "end": v(-29.96, 4.5) * mm});
            skLineSegment(sketch, "E38.13.0.0", {"start": v(-26.39, 5.75) * mm, "end": v(-26.79, 5.75) * mm});
            skLineSegment(sketch, "E38.13.0.1", {"start": v(-26.79, 5.75) * mm, "end": v(-27.19, 5.75) * mm});
            skLineSegment(sketch, "E38.13.0.2", {"start": v(-27.19, 5.75) * mm, "end": v(-27.19, 4.5) * mm});
            skLineSegment(sketch, "E38.13.0.3", {"start": v(-26.39, 4.5) * mm, "end": v(-26.39, 5.75) * mm});
            skLineSegment(sketch, "E38.13.0.4", {"start": v(-27.19, 4.5) * mm, "end": v(-26.39, 4.5) * mm});
            skLineSegment(sketch, "E38.14.0.0", {"start": v(-22.82, 5.75) * mm, "end": v(-23.22, 5.75) * mm});
            skLineSegment(sketch, "E38.14.0.1", {"start": v(-23.22, 5.75) * mm, "end": v(-23.62, 5.75) * mm});
            skLineSegment(sketch, "E38.14.0.2", {"start": v(-23.62, 5.75) * mm, "end": v(-23.62, 4.5) * mm});
            skLineSegment(sketch, "E38.14.0.3", {"start": v(-22.82, 4.5) * mm, "end": v(-22.82, 5.75) * mm});
            skLineSegment(sketch, "E38.14.0.4", {"start": v(-23.62, 4.5) * mm, "end": v(-22.82, 4.5) * mm});
            skLineSegment(sketch, "E38.15.0.0", {"start": v(-19.25, 5.75) * mm, "end": v(-19.65, 5.75) * mm});
            skLineSegment(sketch, "E38.15.0.1", {"start": v(-19.65, 5.75) * mm, "end": v(-20.05, 5.75) * mm});
            skLineSegment(sketch, "E38.15.0.2", {"start": v(-20.05, 5.75) * mm, "end": v(-20.05, 4.5) * mm});
            skLineSegment(sketch, "E38.15.0.3", {"start": v(-19.25, 4.5) * mm, "end": v(-19.25, 5.75) * mm});
            skLineSegment(sketch, "E38.15.0.4", {"start": v(-20.05, 4.5) * mm, "end": v(-19.25, 4.5) * mm});
            skLineSegment(sketch, "E38.16.0.0", {"start": v(-15.68, 5.75) * mm, "end": v(-16.08, 5.75) * mm});
            skLineSegment(sketch, "E38.16.0.1", {"start": v(-16.08, 5.75) * mm, "end": v(-16.48, 5.75) * mm});
            skLineSegment(sketch, "E38.16.0.2", {"start": v(-16.48, 5.75) * mm, "end": v(-16.48, 4.5) * mm});
            skLineSegment(sketch, "E38.16.0.3", {"start": v(-15.68, 4.5) * mm, "end": v(-15.68, 5.75) * mm});
            skLineSegment(sketch, "E38.16.0.4", {"start": v(-16.48, 4.5) * mm, "end": v(-15.68, 4.5) * mm});
            skLineSegment(sketch, "E38.17.0.0", {"start": v(-12.1, 5.75) * mm, "end": v(-12.5, 5.75) * mm});
            skLineSegment(sketch, "E38.17.0.1", {"start": v(-12.5, 5.75) * mm, "end": v(-12.9, 5.75) * mm});
            skLineSegment(sketch, "E38.17.0.2", {"start": v(-12.9, 5.75) * mm, "end": v(-12.9, 4.5) * mm});
            skLineSegment(sketch, "E38.17.0.3", {"start": v(-12.1, 4.5) * mm, "end": v(-12.1, 5.75) * mm});
            skLineSegment(sketch, "E38.17.0.4", {"start": v(-12.9, 4.5) * mm, "end": v(-12.1, 4.5) * mm});
            skLineSegment(sketch, "E38.18.0.0", {"start": v(-8.54, 5.75) * mm, "end": v(-8.94, 5.75) * mm});
            skLineSegment(sketch, "E38.18.0.1", {"start": v(-8.94, 5.75) * mm, "end": v(-9.34, 5.75) * mm});
            skLineSegment(sketch, "E38.18.0.2", {"start": v(-9.34, 5.75) * mm, "end": v(-9.34, 4.5) * mm});
            skLineSegment(sketch, "E38.18.0.3", {"start": v(-8.54, 4.5) * mm, "end": v(-8.54, 5.75) * mm});
            skLineSegment(sketch, "E38.18.0.4", {"start": v(-9.34, 4.5) * mm, "end": v(-8.54, 4.5) * mm});
            skLineSegment(sketch, "E38.19.0.0", {"start": v(-4.97, 5.75) * mm, "end": v(-5.37, 5.75) * mm});
            skLineSegment(sketch, "E38.19.0.1", {"start": v(-5.37, 5.75) * mm, "end": v(-5.77, 5.75) * mm});
            skLineSegment(sketch, "E38.19.0.2", {"start": v(-5.77, 5.75) * mm, "end": v(-5.77, 4.5) * mm});
            skLineSegment(sketch, "E38.19.0.3", {"start": v(-4.97, 4.5) * mm, "end": v(-4.97, 5.75) * mm});
            skLineSegment(sketch, "E38.19.0.4", {"start": v(-5.77, 4.5) * mm, "end": v(-4.97, 4.5) * mm});
            skLineSegment(sketch, "E38.20.0.0", {"start": v(-1.4, 5.75) * mm, "end": v(-1.8, 5.75) * mm});
            skLineSegment(sketch, "E38.20.0.1", {"start": v(-1.8, 5.75) * mm, "end": v(-2.2, 5.75) * mm});
            skLineSegment(sketch, "E38.20.0.2", {"start": v(-2.2, 5.75) * mm, "end": v(-2.2, 4.5) * mm});
            skLineSegment(sketch, "E38.20.0.3", {"start": v(-1.4, 4.5) * mm, "end": v(-1.4, 5.75) * mm});
            skLineSegment(sketch, "E38.20.0.4", {"start": v(-2.2, 4.5) * mm, "end": v(-1.4, 4.5) * mm});
            skLineSegment(sketch, "E38.direction1", {"start": v(-73.2, 5.75) * mm, "end": v(-69.63, 5.75) * mm, "construction": true});
            skSolve(sketch);
        }
        {
            var Q0;
            Q0 = qSketchRegion(id + "F8", true);
            extrude(context, id + "F9", {"entities" : qUnion([Q0]), "operationType" : NewBodyOperationType.ADD, "oppositeDirection" : true, "depth" : 2.25 * mm, "offsetDistance" : 25 * mm});
        }
        {
            var Q0;
            Q0=makeQuery(id+"F1.opExtrude","SWEPT_FACE",FACE,{"disambiguationData":[OSD([sQuery(id+"F0.wireOp",EDGE,"E7")])]});
            var sketch = newSketch(context, id + "F10", { "sketchPlane" : qUnion([Q0])});
            skLineSegment(sketch, "E39", {"start": v(1.75, 3.83) * mm, "end": v(1.75, 6.83) * mm, "construction": true});
            skLineSegment(sketch, "E40.bottom", {"start": v(0.53, 5.53) * mm, "end": v(2.96, 5.53) * mm});
            skLineSegment(sketch, "E40.top", {"start": v(0.53, 5.12) * mm, "end": v(2.96, 5.12) * mm});
            skLineSegment(sketch, "E40.left", {"start": v(0.53, 5.53) * mm, "end": v(0.53, 5.12) * mm});
            skLineSegment(sketch, "E40.right", {"start": v(2.96, 5.53) * mm, "end": v(2.96, 5.12) * mm});
            skPoint(sketch, "E40.middle", {"position": v(1.75, 5.33) * mm});
            skLineSegment(sketch, "E41.1.0.0", {"start": v(4.1, 5.12) * mm, "end": v(6.53, 5.12) * mm});
            skLineSegment(sketch, "E41.1.0.1", {"start": v(4.1, 5.53) * mm, "end": v(6.53, 5.53) * mm});
            skLineSegment(sketch, "E41.1.0.2", {"start": v(4.1, 5.53) * mm, "end": v(4.1, 5.12) * mm});
            skLineSegment(sketch, "E41.1.0.3", {"start": v(6.53, 5.53) * mm, "end": v(6.53, 5.12) * mm});
            skLineSegment(sketch, "E41.2.0.0", {"start": v(7.67, 5.12) * mm, "end": v(10.1, 5.12) * mm});
            skLineSegment(sketch, "E41.2.0.1", {"start": v(7.67, 5.53) * mm, "end": v(10.1, 5.53) * mm});
            skLineSegment(sketch, "E41.2.0.2", {"start": v(7.67, 5.53) * mm, "end": v(7.67, 5.12) * mm});
            skLineSegment(sketch, "E41.2.0.3", {"start": v(10.1, 5.53) * mm, "end": v(10.1, 5.12) * mm});
            skLineSegment(sketch, "E41.3.0.0", {"start": v(11.24, 5.12) * mm, "end": v(13.67, 5.12) * mm});
            skLineSegment(sketch, "E41.3.0.1", {"start": v(11.24, 5.53) * mm, "end": v(13.67, 5.53) * mm});
            skLineSegment(sketch, "E41.3.0.2", {"start": v(11.24, 5.53) * mm, "end": v(11.24, 5.12) * mm});
            skLineSegment(sketch, "E41.3.0.3", {"start": v(13.67, 5.53) * mm, "end": v(13.67, 5.12) * mm});
            skLineSegment(sketch, "E41.4.0.0", {"start": v(14.81, 5.12) * mm, "end": v(17.24, 5.12) * mm});
            skLineSegment(sketch, "E41.4.0.1", {"start": v(14.81, 5.53) * mm, "end": v(17.24, 5.53) * mm});
            skLineSegment(sketch, "E41.4.0.2", {"start": v(14.81, 5.53) * mm, "end": v(14.81, 5.12) * mm});
            skLineSegment(sketch, "E41.4.0.3", {"start": v(17.24, 5.53) * mm, "end": v(17.24, 5.12) * mm});
            skLineSegment(sketch, "E41.5.0.0", {"start": v(18.38, 5.12) * mm, "end": v(20.81, 5.12) * mm});
            skLineSegment(sketch, "E41.5.0.1", {"start": v(18.38, 5.53) * mm, "end": v(20.81, 5.53) * mm});
            skLineSegment(sketch, "E41.5.0.2", {"start": v(18.38, 5.53) * mm, "end": v(18.38, 5.12) * mm});
            skLineSegment(sketch, "E41.5.0.3", {"start": v(20.81, 5.53) * mm, "end": v(20.81, 5.12) * mm});
            skLineSegment(sketch, "E41.6.0.0", {"start": v(21.95, 5.12) * mm, "end": v(24.38, 5.12) * mm});
            skLineSegment(sketch, "E41.6.0.1", {"start": v(21.95, 5.53) * mm, "end": v(24.38, 5.53) * mm});
            skLineSegment(sketch, "E41.6.0.2", {"start": v(21.95, 5.53) * mm, "end": v(21.95, 5.12) * mm});
            skLineSegment(sketch, "E41.6.0.3", {"start": v(24.38, 5.53) * mm, "end": v(24.38, 5.12) * mm});
            skLineSegment(sketch, "E41.7.0.0", {"start": v(25.52, 5.12) * mm, "end": v(27.95, 5.12) * mm});
            skLineSegment(sketch, "E41.7.0.1", {"start": v(25.52, 5.53) * mm, "end": v(27.95, 5.53) * mm});
            skLineSegment(sketch, "E41.7.0.2", {"start": v(25.52, 5.53) * mm, "end": v(25.52, 5.12) * mm});
            skLineSegment(sketch, "E41.7.0.3", {"start": v(27.95, 5.53) * mm, "end": v(27.95, 5.12) * mm});
            skLineSegment(sketch, "E41.8.0.0", {"start": v(29.1, 5.12) * mm, "end": v(31.52, 5.12) * mm});
            skLineSegment(sketch, "E41.8.0.1", {"start": v(29.1, 5.53) * mm, "end": v(31.52, 5.53) * mm});
            skLineSegment(sketch, "E41.8.0.2", {"start": v(29.1, 5.53) * mm, "end": v(29.1, 5.12) * mm});
            skLineSegment(sketch, "E41.8.0.3", {"start": v(31.52, 5.53) * mm, "end": v(31.52, 5.12) * mm});
            skLineSegment(sketch, "E41.9.0.0", {"start": v(32.66, 5.12) * mm, "end": v(35.1, 5.12) * mm});
            skLineSegment(sketch, "E41.9.0.1", {"start": v(32.66, 5.53) * mm, "end": v(35.1, 5.53) * mm});
            skLineSegment(sketch, "E41.9.0.2", {"start": v(32.66, 5.53) * mm, "end": v(32.66, 5.12) * mm});
            skLineSegment(sketch, "E41.9.0.3", {"start": v(35.1, 5.53) * mm, "end": v(35.1, 5.12) * mm});
            skLineSegment(sketch, "E41.10.0.0", {"start": v(36.23, 5.12) * mm, "end": v(38.66, 5.12) * mm});
            skLineSegment(sketch, "E41.10.0.1", {"start": v(36.23, 5.53) * mm, "end": v(38.66, 5.53) * mm});
            skLineSegment(sketch, "E41.10.0.2", {"start": v(36.23, 5.53) * mm, "end": v(36.23, 5.12) * mm});
            skLineSegment(sketch, "E41.10.0.3", {"start": v(38.66, 5.53) * mm, "end": v(38.66, 5.12) * mm});
            skLineSegment(sketch, "E41.11.0.0", {"start": v(39.8, 5.12) * mm, "end": v(42.23, 5.12) * mm});
            skLineSegment(sketch, "E41.11.0.1", {"start": v(39.8, 5.53) * mm, "end": v(42.23, 5.53) * mm});
            skLineSegment(sketch, "E41.11.0.2", {"start": v(39.8, 5.53) * mm, "end": v(39.8, 5.12) * mm});
            skLineSegment(sketch, "E41.11.0.3", {"start": v(42.23, 5.53) * mm, "end": v(42.23, 5.12) * mm});
            skLineSegment(sketch, "E41.12.0.0", {"start": v(43.37, 5.12) * mm, "end": v(45.8, 5.12) * mm});
            skLineSegment(sketch, "E41.12.0.1", {"start": v(43.37, 5.53) * mm, "end": v(45.8, 5.53) * mm});
            skLineSegment(sketch, "E41.12.0.2", {"start": v(43.37, 5.53) * mm, "end": v(43.37, 5.12) * mm});
            skLineSegment(sketch, "E41.12.0.3", {"start": v(45.8, 5.53) * mm, "end": v(45.8, 5.12) * mm});
            skLineSegment(sketch, "E41.13.0.0", {"start": v(46.94, 5.12) * mm, "end": v(49.37, 5.12) * mm});
            skLineSegment(sketch, "E41.13.0.1", {"start": v(46.94, 5.53) * mm, "end": v(49.37, 5.53) * mm});
            skLineSegment(sketch, "E41.13.0.2", {"start": v(46.94, 5.53) * mm, "end": v(46.94, 5.12) * mm});
            skLineSegment(sketch, "E41.13.0.3", {"start": v(49.37, 5.53) * mm, "end": v(49.37, 5.12) * mm});
            skLineSegment(sketch, "E41.14.0.0", {"start": v(50.51, 5.12) * mm, "end": v(52.94, 5.12) * mm});
            skLineSegment(sketch, "E41.14.0.1", {"start": v(50.51, 5.53) * mm, "end": v(52.94, 5.53) * mm});
            skLineSegment(sketch, "E41.14.0.2", {"start": v(50.51, 5.53) * mm, "end": v(50.51, 5.12) * mm});
            skLineSegment(sketch, "E41.14.0.3", {"start": v(52.94, 5.53) * mm, "end": v(52.94, 5.12) * mm});
            skLineSegment(sketch, "E41.15.0.0", {"start": v(54.08, 5.12) * mm, "end": v(56.51, 5.12) * mm});
            skLineSegment(sketch, "E41.15.0.1", {"start": v(54.08, 5.53) * mm, "end": v(56.51, 5.53) * mm});
            skLineSegment(sketch, "E41.15.0.2", {"start": v(54.08, 5.53) * mm, "end": v(54.08, 5.12) * mm});
            skLineSegment(sketch, "E41.15.0.3", {"start": v(56.51, 5.53) * mm, "end": v(56.51, 5.12) * mm});
            skLineSegment(sketch, "E41.16.0.0", {"start": v(57.65, 5.12) * mm, "end": v(60.08, 5.12) * mm});
            skLineSegment(sketch, "E41.16.0.1", {"start": v(57.65, 5.53) * mm, "end": v(60.08, 5.53) * mm});
            skLineSegment(sketch, "E41.16.0.2", {"start": v(57.65, 5.53) * mm, "end": v(57.65, 5.12) * mm});
            skLineSegment(sketch, "E41.16.0.3", {"start": v(60.08, 5.53) * mm, "end": v(60.08, 5.12) * mm});
            skLineSegment(sketch, "E41.17.0.0", {"start": v(61.22, 5.12) * mm, "end": v(63.65, 5.12) * mm});
            skLineSegment(sketch, "E41.17.0.1", {"start": v(61.22, 5.53) * mm, "end": v(63.65, 5.53) * mm});
            skLineSegment(sketch, "E41.17.0.2", {"start": v(61.22, 5.53) * mm, "end": v(61.22, 5.12) * mm});
            skLineSegment(sketch, "E41.17.0.3", {"start": v(63.65, 5.53) * mm, "end": v(63.65, 5.12) * mm});
            skLineSegment(sketch, "E41.18.0.0", {"start": v(64.8, 5.12) * mm, "end": v(67.22, 5.12) * mm});
            skLineSegment(sketch, "E41.18.0.1", {"start": v(64.8, 5.53) * mm, "end": v(67.22, 5.53) * mm});
            skLineSegment(sketch, "E41.18.0.2", {"start": v(64.8, 5.53) * mm, "end": v(64.8, 5.12) * mm});
            skLineSegment(sketch, "E41.18.0.3", {"start": v(67.22, 5.53) * mm, "end": v(67.22, 5.12) * mm});
            skLineSegment(sketch, "E41.19.0.0", {"start": v(68.36, 5.12) * mm, "end": v(70.8, 5.12) * mm});
            skLineSegment(sketch, "E41.19.0.1", {"start": v(68.36, 5.53) * mm, "end": v(70.8, 5.53) * mm});
            skLineSegment(sketch, "E41.19.0.2", {"start": v(68.36, 5.53) * mm, "end": v(68.36, 5.12) * mm});
            skLineSegment(sketch, "E41.19.0.3", {"start": v(70.8, 5.53) * mm, "end": v(70.8, 5.12) * mm});
            skLineSegment(sketch, "E41.20.0.0", {"start": v(71.93, 5.12) * mm, "end": v(74.36, 5.12) * mm});
            skLineSegment(sketch, "E41.20.0.1", {"start": v(71.93, 5.53) * mm, "end": v(74.36, 5.53) * mm});
            skLineSegment(sketch, "E41.20.0.2", {"start": v(71.93, 5.53) * mm, "end": v(71.93, 5.12) * mm});
            skLineSegment(sketch, "E41.20.0.3", {"start": v(74.36, 5.53) * mm, "end": v(74.36, 5.12) * mm});
            skLineSegment(sketch, "E41.direction1", {"start": v(0.53, 5.12) * mm, "end": v(4.1, 5.12) * mm, "construction": true});
            skSolve(sketch);
        }
        {
            var Q0;
            Q0 = qSketchRegion(id + "F10", true);
            extrude(context, id + "F11", {"entities" : qUnion([Q0]), "operationType" : NewBodyOperationType.REMOVE, "oppositeDirection" : true, "depth" : 5 * mm, "offsetDistance" : 25 * mm});
        }
    });
